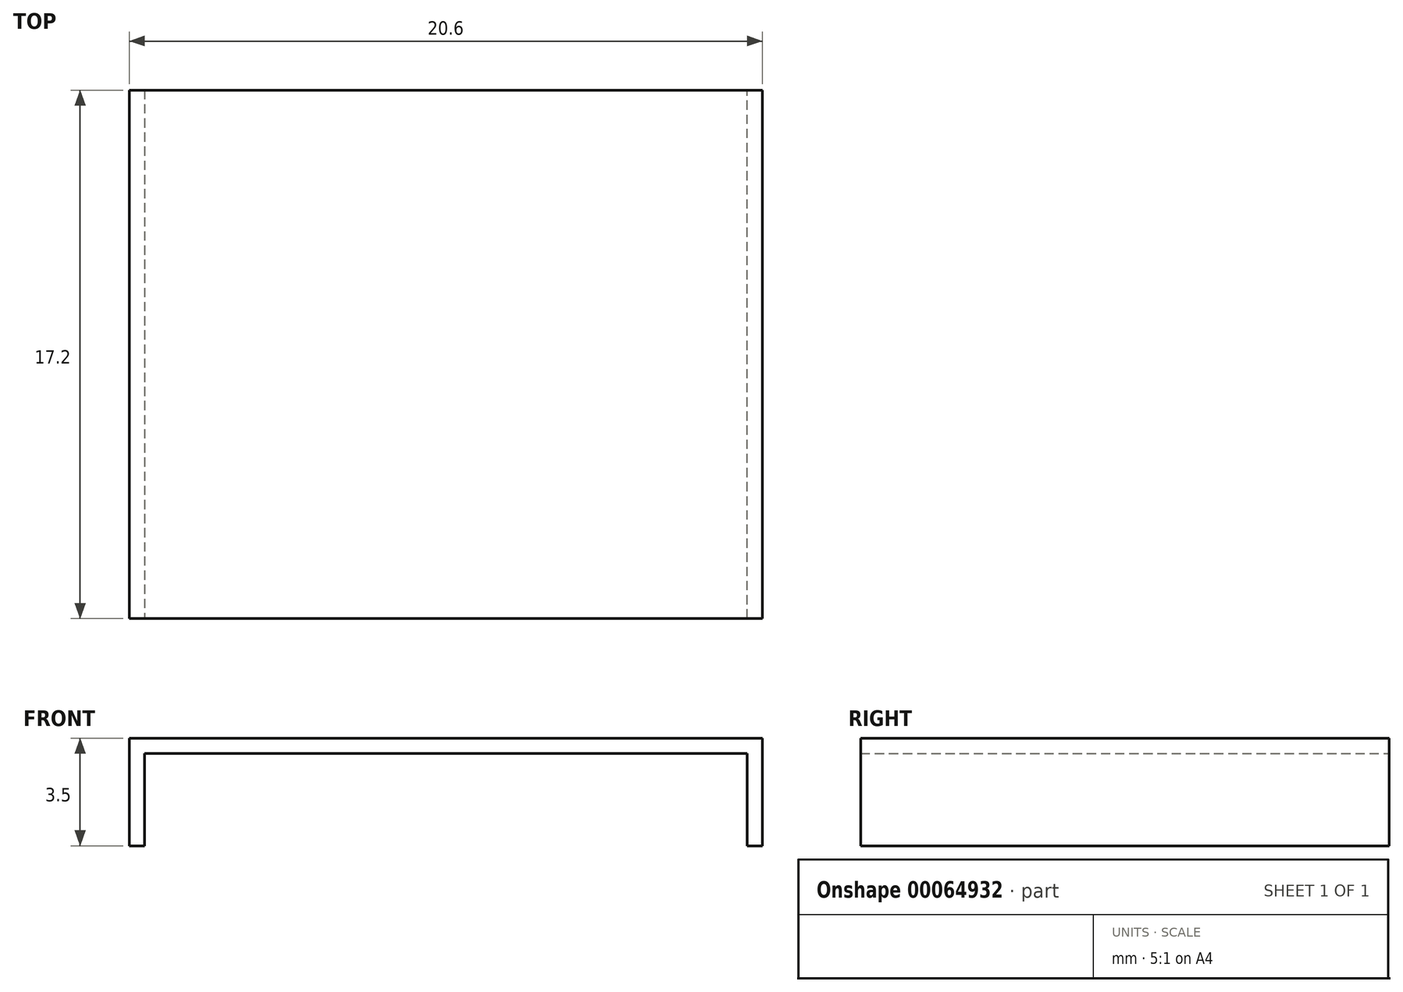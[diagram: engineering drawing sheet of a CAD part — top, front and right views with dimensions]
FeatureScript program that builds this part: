
annotation { "Feature Type Name" : "Feature", "Feature Type Description" : "" }
export const myFeature = defineFeature(function(context is Context, id is Id, definition is map)
    precondition{}
    {
        {
            var Q0;
            Q0=qCreatedBy(makeId("Top.planeOp"),FACE);
            var sketch = newSketch(context, id + "F0", { "sketchPlane" : qUnion([Q0])});
            skLineSegment(sketch, "E0.bottom", {"start": v(0, 0) * mm, "end": v(20.6, 0) * mm});
            skLineSegment(sketch, "E0.top", {"start": v(0, 17.2) * mm, "end": v(20.6, 17.2) * mm});
            skLineSegment(sketch, "E0.left", {"start": v(0, 0) * mm, "end": v(0, 17.2) * mm});
            skLineSegment(sketch, "E0.right", {"start": v(20.6, 0) * mm, "end": v(20.6, 17.2) * mm});
            skSolve(sketch);
        }
        {
            var Q0;
            Q0=makeQuery(id+"F0.imprint","IMPRINT",FACE,{"disambiguationData":[TD([[makeQuery(id+"F0.imprint","IMPRINT",EDGE,{"derivedFrom":sQuery(id+"F0.wireOp",EDGE,"E0.bottom")}),1.0]])]});
            extrude(context, id + "F1", {"entities" : qUnion([Q0]), "depth" : .5 * mm});
        }
        {
            var Q0;
            Q0=makeQuery(id+"F1.opExtrude","CAP_FACE",FACE,{"disambiguationData":[OSD([sQuery(id+"F0.wireOp",EDGE,"E0.bottom"),sQuery(id+"F0.wireOp",EDGE,"E0.top"),sQuery(id+"F0.wireOp",EDGE,"E0.left"),sQuery(id+"F0.wireOp",EDGE,"E0.right")])],"isStart":true});
            var sketch = newSketch(context, id + "F2", { "sketchPlane" : qUnion([Q0])});
            skLineSegment(sketch, "E1", {"start": v(0, 0) * mm, "end": v(0, -17.2) * mm});
            skLineSegment(sketch, "E2", {"start": v(0, -17.2) * mm, "end": v(0.5, -17.2) * mm});
            skLineSegment(sketch, "E3", {"start": v(0.5, -17.2) * mm, "end": v(0.5, 0) * mm});
            skLineSegment(sketch, "E4", {"start": v(0.5, 0) * mm, "end": v(0, 0) * mm});
            skLineSegment(sketch, "E5", {"start": v(20.6, 0) * mm, "end": v(20.1, 0) * mm});
            skLineSegment(sketch, "E6", {"start": v(20.1, 0) * mm, "end": v(20.1, -17.2) * mm});
            skLineSegment(sketch, "E7", {"start": v(20.1, -17.2) * mm, "end": v(20.6, -17.2) * mm});
            skLineSegment(sketch, "E8", {"start": v(20.6, -17.2) * mm, "end": v(20.6, 0) * mm});
            skSolve(sketch);
        }
        {
            var Q0;
            Q0=makeQuery(id+"F2.imprint","IMPRINT",FACE,{"disambiguationData":[TD([[makeQuery(id+"F2.imprint","IMPRINT",EDGE,{"derivedFrom":sQuery(id+"F2.wireOp",EDGE,"E1")}),1.0]])]});
            var Q1;
            Q1=makeQuery(id+"F2.imprint","IMPRINT",FACE,{"disambiguationData":[TD([[makeQuery(id+"F2.imprint","IMPRINT",EDGE,{"derivedFrom":sQuery(id+"F2.wireOp",EDGE,"E5")}),-1.0]])]});
            extrude(context, id + "F3", {"entities" : qUnion([Q0, Q1]), "operationType" : NewBodyOperationType.ADD, "depth" : 3 * mm});
        }
    });
